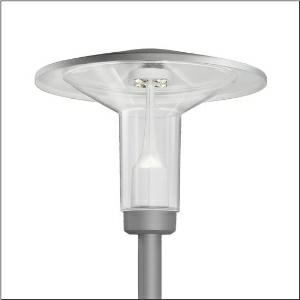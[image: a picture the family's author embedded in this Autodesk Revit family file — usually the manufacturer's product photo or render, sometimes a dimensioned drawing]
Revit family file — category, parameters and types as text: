
# Revit family: laterne_iq___p1_0a_5xa5255ff14h_2151
name_source: partatom
category: Lighting Fixtures
units: mm (PartAtom-declared; Revit-internal decimal feet)

## family parameters
Cut with Voids When Loaded = No
Host = Face
Light Source = No
Part Type = Normal
Room Calculation Point = No
Round Connector Dimension = Use Diameter
Shared = No

## types (1)
- --- (1 x LED, 1510 lm, 10.5 W, 3000K)
    Apparent Load = 11 VA
    CIE Flux Codes = 35 64 91 96 100
    Color Rendering = 70
    Color Temperature = 3000K
    Default Elevation = 1800 mm
    Description = Lantern iQ, mast luminaire, Module 540 iQ-SR, primary light control with 3 zone facetted reflector, of plastic, silver coated, highly specular, structured, primary optical cover: cover, of PMMA, transparent, light distribution: P1.0a, light emission: direct distribution, primary light characteristic: strongly asymmetric, installation type: post-top, LED, High Power LED, rated luminous flux: 1.510lm, luminous efficacy: 144lm/W, light colour: 730, colour temperature: 3000K, control gear: iQ Street-Remote, control: Auto-Match, Temp-Guard, Lumen-Switch, Night-Set, Smart-Wire, Light-Fading, Desk-Remote (wireless, voltage-free reading and setting of iQ features in the workshop via application-optimized NFC function/RFID function), optimised constant luminous flux control (CLO 2.0), Street-Remote, pre-setting: logarithmic dimming characteristic, with terminal, 6-pole, max. 2.5mm², mains connection: 230..240V, AC, 50/60Hz, start of lifetime: 11W, end of service life: 11W, reduction: 5W, luminaire housing, upper part, of glass-fibre reinforced polyester, coated, Siteco® metallic grey (DB 702S), diameter: 750mm, height: 583mm, spigot size: d x l = 76 x 70mm (post-top) | with reducer (optional accessory) 60 x 70mm, mounting height: 3..5m, post-top mast mounting element, of diecast aluminium, coated, Siteco® metallic grey (DB 702S), Module 540 iQ-SR, traffic white (RAL 9016), equipment: standard, protection rating (complete): IP65, insulation class (complete): insulation class II (safety insulation), certification: CE, ENEC, VDE, packaging unit: 1 piece

Light Distribution: P1.0a
    Height = 583 mm
    Lamp = 1 x LED
    Lamp Light Flux = 1510 lm
    Lamp Power = 10.5 W
    Lamp count = 1
    Length = 750 mm
    Luminous efficacy = 144 lm/W
    Manufacturer = Siteco
    ModVariant = No
    Model = 5XA5255FF14H
    Number of Poles = 1
    OnlyDefault = Yes
    Power Factor = 1
    Product Name = Laterne iQ | P1.0a
    Product group = mast luminaire | pylon top
    ProductGroupID = 6100
    Protection Class = Protection class II
    Protection Degree = IP 65
    RLX_Detail_Level = 1
    RLX_Emergency_Light_Flux = 0 lm
    RLX_Emergency_Type = 0
    RLX_Emergency_Type_DB = No
    RlxData = <blob elided: 59253 chars, md5=520e269c>
    Socket = socket
    Standby Power = 0 W
    System Light Flux = 1510 lm
    System Power = 11 W
    Type Comments = factory setting: luminous flux: 100 % | dim-lin: 254 | 419 mA
    Type Image = l_1006050.jpg
    URL = http://relux.com
    VarID = @adj_160530
    Voltage = 0 V
    Weight = 0.00 kg
    Width = 0 mm  [stored 0 ft]

note: [stored X ft] marks values corroborated as IEEE doubles in the binary element streams (Revit-internal decimal feet)

## geometry (parser evidence)
native form markers: Blend x4, Sweep x13
no freeform markers — native parametric forms only
